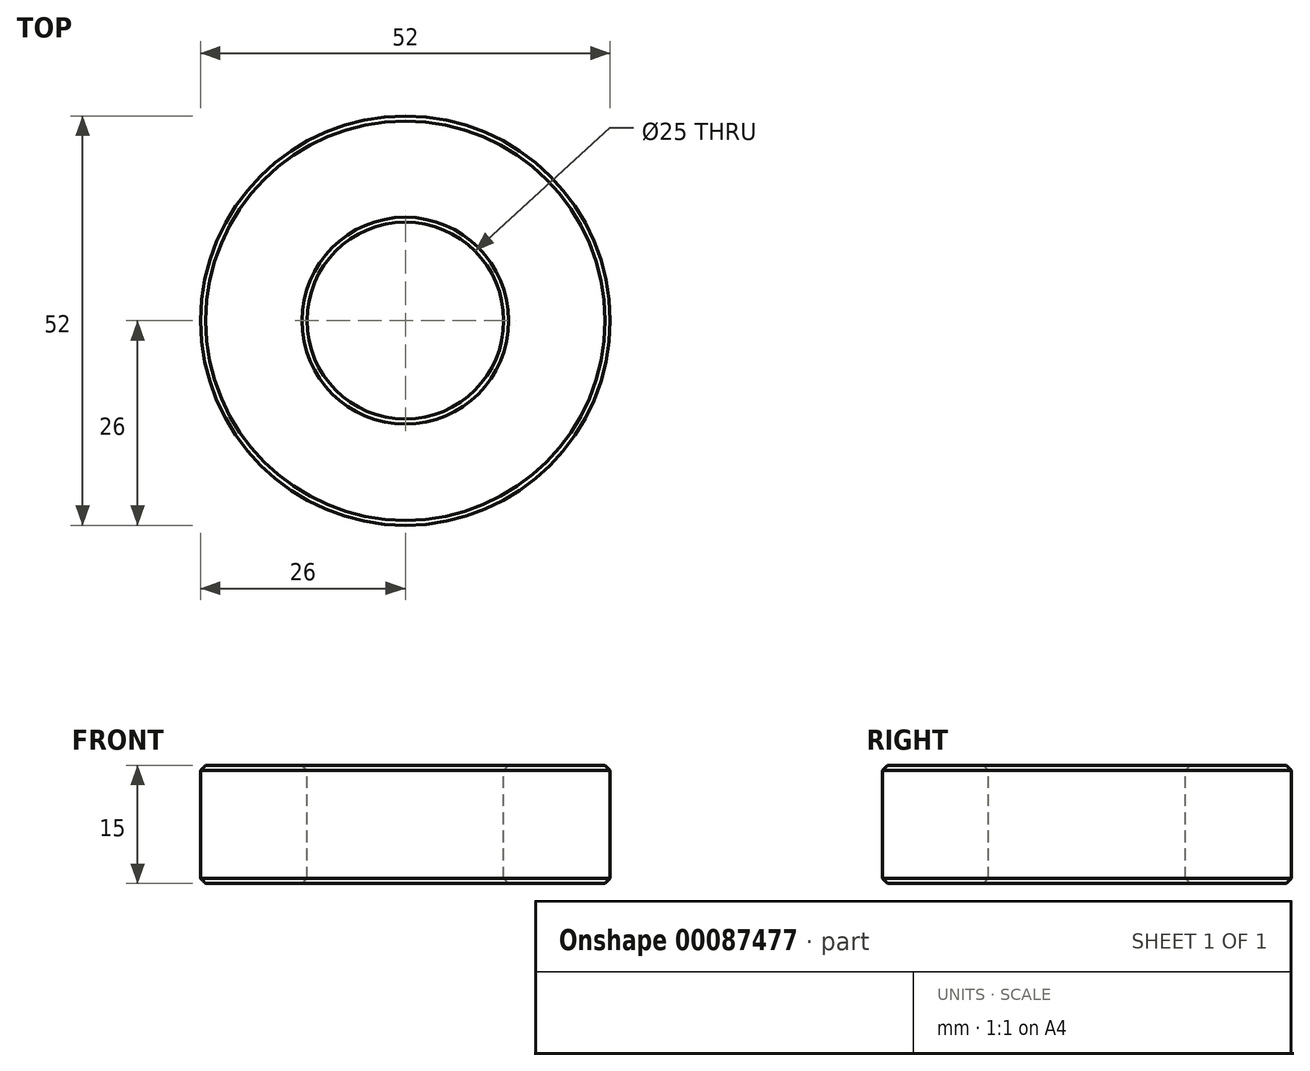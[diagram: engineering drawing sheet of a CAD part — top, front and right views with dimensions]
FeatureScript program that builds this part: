
annotation { "Feature Type Name" : "Feature", "Feature Type Description" : "" }
export const myFeature = defineFeature(function(context is Context, id is Id, definition is map)
    precondition{}
    {
        {
            var Q0;
            Q0=qCreatedBy(makeId("Front.planeOp"),FACE);
            var sketch = newSketch(context, id + "F0", { "sketchPlane" : qUnion([Q0])});
            skLineSegment(sketch, "E0", {"start": v(-26, 7.5) * mm, "end": v(-26, -7.5) * mm});
            skLineSegment(sketch, "E1", {"start": v(-26, -7.5) * mm, "end": v(-12.5, -7.5) * mm});
            skLineSegment(sketch, "E2", {"start": v(-12.5, -7.5) * mm, "end": v(-12.5, 7.5) * mm});
            skLineSegment(sketch, "E3", {"start": v(-26, 7.5) * mm, "end": v(-12.5, 7.5) * mm});
            skLineSegment(sketch, "E4", {"start": v(0, 26) * mm, "end": v(0, -19.2) * mm});
            skSolve(sketch);
        }
        {
            var Q0;
            Q0 = qSketchRegion(id + "F0", true);
            var Q1;
            Q1=sQuery(id+"F0.wireOp",EDGE,"E4");
            revolve(context, id + "F1", {"entities" : qUnion([Q0]), "axis" : qUnion([Q1]), "revolveType" : RevolveType.FULL});
        }
        {
            var Q0;
            Q0=makeQuery(id+"F1.opRevolve","SWEPT_EDGE",EDGE,{"disambiguationData":[OSD([sQuery(id+"F0.wireOp",EDGE,"E0"),sQuery(id+"F0.wireOp",EDGE,"E3")])]});
            var Q1;
            Q1=makeQuery(id+"F1.opRevolve","SWEPT_EDGE",EDGE,{"disambiguationData":[OSD([sQuery(id+"F0.wireOp",EDGE,"E0"),sQuery(id+"F0.wireOp",EDGE,"E1")])]});
            var Q2;
            Q2=makeQuery(id+"F1.opRevolve","SWEPT_EDGE",EDGE,{"disambiguationData":[OSD([sQuery(id+"F0.wireOp",EDGE,"E2"),sQuery(id+"F0.wireOp",EDGE,"E3")])]});
            var Q3;
            Q3=makeQuery(id+"F1.opRevolve","SWEPT_EDGE",EDGE,{"disambiguationData":[OSD([sQuery(id+"F0.wireOp",EDGE,"E1"),sQuery(id+"F0.wireOp",EDGE,"E2")])]});
            chamfer(context, id + "F2", {"entities" : qUnion([Q0, Q1, Q2, Q3]), "width" : 0.64 * mm, "tangentPropagation" : true});
        }
    });
